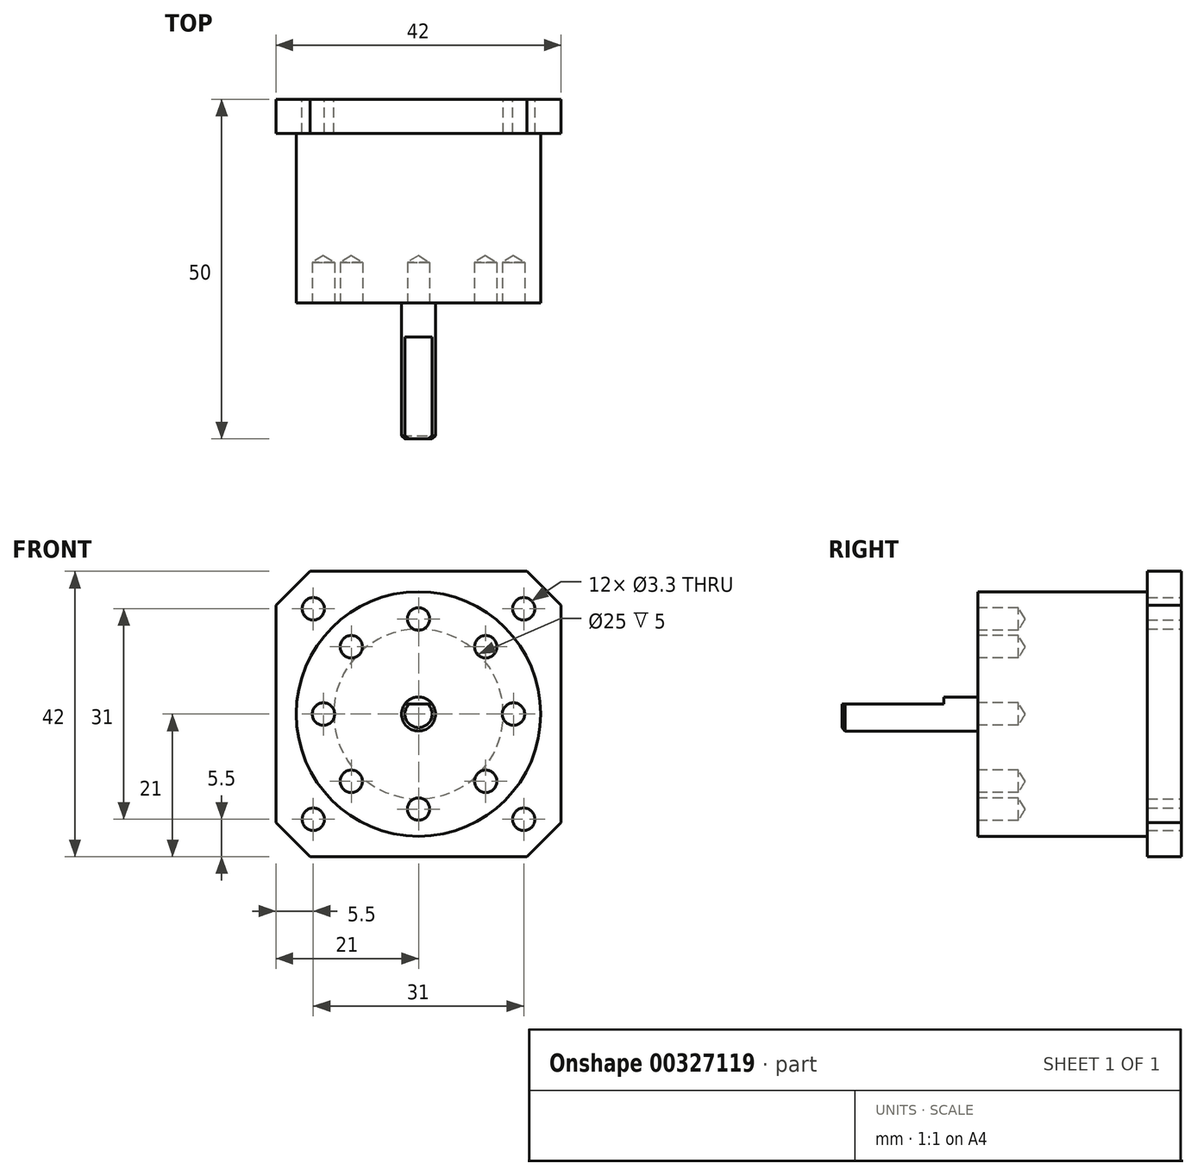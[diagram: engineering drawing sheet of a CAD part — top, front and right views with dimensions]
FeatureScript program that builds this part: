
annotation { "Feature Type Name" : "Feature", "Feature Type Description" : "" }
export const myFeature = defineFeature(function(context is Context, id is Id, definition is map)
    precondition{}
    {
        {
            var Q0;
            Q0=qCreatedBy(makeId("Front.planeOp"),FACE);
            var sketch = newSketch(context, id + "F0", { "sketchPlane" : qUnion([Q0])});
            skLineSegment(sketch, "E0.bottom", {"start": v(21, 21) * mm, "end": v(-21, 21) * mm});
            skLineSegment(sketch, "E0.top", {"start": v(21, -21) * mm, "end": v(-21, -21) * mm});
            skLineSegment(sketch, "E0.left", {"start": v(21, 21) * mm, "end": v(21, -21) * mm});
            skLineSegment(sketch, "E0.right", {"start": v(-21, 21) * mm, "end": v(-21, -21) * mm});
            skPoint(sketch, "E0.middle", {"position": v(0, 0) * mm});
            skLineSegment(sketch, "E1.bottom", {"start": v(-15.5, 15.5) * mm, "end": v(15.5, 15.5) * mm, "construction": true});
            skLineSegment(sketch, "E1.top", {"start": v(-15.5, -15.5) * mm, "end": v(15.5, -15.5) * mm, "construction": true});
            skLineSegment(sketch, "E1.left", {"start": v(-15.5, 15.5) * mm, "end": v(-15.5, -15.5) * mm, "construction": true});
            skLineSegment(sketch, "E1.right", {"start": v(15.5, 15.5) * mm, "end": v(15.5, -15.5) * mm, "construction": true});
            skCircle(sketch, "E2", {"center": v(0, 0) * mm, "radius": 12.5 * mm});
            skSolve(sketch);
        }
        {
            var Q0;
            Q0=makeQuery(id+"F0.imprint","IMPRINT",FACE,{"disambiguationData":[TD([[makeQuery(id+"F0.imprint","IMPRINT",EDGE,{"derivedFrom":sQuery(id+"F0.wireOp",EDGE,"E0.bottom")}),1.0]])]});
            extrude(context, id + "F1", {"entities" : qUnion([Q0]), "depth" : 5 * mm});
        }
        {
            var Q0;
            Q0=makeQuery(id+"F1.opExtrude","CAP_FACE",FACE,{"disambiguationData":[OSD([sQuery(id+"F0.wireOp",EDGE,"E0.bottom"),sQuery(id+"F0.wireOp",EDGE,"E0.top"),sQuery(id+"F0.wireOp",EDGE,"E0.left"),sQuery(id+"F0.wireOp",EDGE,"E0.right"),sQuery(id+"F0.wireOp",EDGE,"E2")])],"isStart":false});
            var sketch = newSketch(context, id + "F2", { "sketchPlane" : qUnion([Q0])});
            skCircle(sketch, "E3", {"center": v(0, 0) * mm, "radius": 18 * mm});
            skSolve(sketch);
        }
        {
            var Q0;
            Q0=makeQuery(id+"F2.imprint","IMPRINT",FACE,{"disambiguationData":[TD([[makeQuery(id+"F2.imprint","IMPRINT",EDGE,{"derivedFrom":sQuery(id+"F2.wireOp",EDGE,"E3")}),1.0]])]});
            var Q1;
            Q1=makeQuery(id+"F2.imprint","IMPRINT",FACE,{"disambiguationData":[TD([[makeQuery(id+"F2.imprint","IMPRINT",EDGE,{"derivedFrom":makeQuery(id+"F1.opExtrude","CAP_EDGE",EDGE,{"disambiguationData":[OSD([sQuery(id+"F0.wireOp",EDGE,"E2")])],"isStart":false})}),1.0]])]});
            extrude(context, id + "F3", {"entities" : qUnion([Q0, Q1]), "operationType" : NewBodyOperationType.ADD, "depth" : 25 * mm});
        }
        {
            var Q0;
            Q0=makeQuery(id+"F3.opExtrude","CAP_FACE",FACE,{"disambiguationData":[OSD([sQuery(id+"F2.wireOp",EDGE,"E3")])],"isStart":false});
            var sketch = newSketch(context, id + "F4", { "sketchPlane" : qUnion([Q0])});
            skCircle(sketch, "E4.cCircle", {"center": v(0, 0) * mm, "radius": 14 * mm, "construction": true});
            skLineSegment(sketch, "E4.0", {"start": v(0, 14) * mm, "end": v(14, 0) * mm, "construction": true});
            skLineSegment(sketch, "E4.1", {"start": v(14, 0) * mm, "end": v(0, -14) * mm, "construction": true});
            skLineSegment(sketch, "E4.2", {"start": v(0, -14) * mm, "end": v(-14, 0) * mm, "construction": true});
            skLineSegment(sketch, "E4.3", {"start": v(-14, 0) * mm, "end": v(0, 14) * mm, "construction": true});
            skCircle(sketch, "E5", {"center": v(0, 0) * mm, "radius": 2.5 * mm});
            skLineSegment(sketch, "E6.bottom", {"start": v(9.9, 9.9) * mm, "end": v(-9.9, 9.9) * mm, "construction": true});
            skLineSegment(sketch, "E6.top", {"start": v(9.9, -9.9) * mm, "end": v(-9.9, -9.9) * mm, "construction": true});
            skLineSegment(sketch, "E6.left", {"start": v(9.9, 9.9) * mm, "end": v(9.9, -9.9) * mm, "construction": true});
            skLineSegment(sketch, "E6.right", {"start": v(-9.9, 9.9) * mm, "end": v(-9.9, -9.9) * mm, "construction": true});
            skSolve(sketch);
        }
        {
            var Q0;
            Q0=makeQuery(id+"F4.imprint","IMPRINT",FACE,{"disambiguationData":[TD([[makeQuery(id+"F4.imprint","IMPRINT",EDGE,{"derivedFrom":sQuery(id+"F4.wireOp",EDGE,"E5")}),1.0]])]});
            extrude(context, id + "F5", {"entities" : qUnion([Q0]), "operationType" : NewBodyOperationType.ADD, "depth" : 20 * mm});
        }
        {
            var Q0;
            Q0=makeQuery(id+"F5.opExtrude","CAP_FACE",FACE,{"disambiguationData":[OSD([sQuery(id+"F4.wireOp",EDGE,"E5")])],"isStart":false});
            var sketch = newSketch(context, id + "F6", { "sketchPlane" : qUnion([Q0])});
            skLineSegment(sketch, "E7", {"start": v(2, 1.5) * mm, "end": v(-2, 1.5) * mm});
            skSolve(sketch);
        }
        {
            var Q0;
            {var subQ0=sQuery(id+"F6.wireOp",EDGE,"E7");Q0=makeQuery(id+"F6.imprint","IMPRINT",FACE,{"disambiguationData":[TD([[makeQuery(id+"F6.imprint","IMPRINT",EDGE,{"derivedFrom":subQ0}),-1.0]])]});}
            extrude(context, id + "F7", {"entities" : qUnion([Q0]), "operationType" : NewBodyOperationType.REMOVE, "oppositeDirection" : true, "depth" : 15 * mm});
        }
        {
            var Q0;
            Q0=sQuery(id+"F0.wireOp",VERTEX,"E1.left.start");
            var Q1;
            Q1=sQuery(id+"F0.wireOp",VERTEX,"E1.right.start");
            var Q2;
            Q2=sQuery(id+"F0.wireOp",VERTEX,"E1.left.end");
            var Q3;
            Q3=sQuery(id+"F0.wireOp",VERTEX,"E1.right.end");
            var Q4;
            Q4=makeQuery(id+"F1.opExtrude","SWEPT_BODY",BODY,{"disambiguationData":[OSD([sQuery(id+"F0.wireOp",EDGE,"E0.bottom"),sQuery(id+"F0.wireOp",EDGE,"E0.top"),sQuery(id+"F0.wireOp",EDGE,"E0.left"),sQuery(id+"F0.wireOp",EDGE,"E0.right"),sQuery(id+"F0.wireOp",EDGE,"E2")])]});
            hole(context, id + "F8", {"style" : HoleStyle.SIMPLE, "endStyle" : HoleEndStyle.THROUGH, "oppositeDirection" : true, "standardTappedOrClearance" : lookupTablePath({ "standard" : "ISO", "fit" : "Normal", "size" : "M3", "type" : "Clearance" }), "standardBlindInLast" : lookupTablePath({ "fit" : "Standard", "standard" : "ISO", "size" : "M3", "type" : "Clearance" }), "holeDiameter" : 3.3 * mm, "tappedDepth" : 12 * mm, "tapClearance" : 3, "locations" : qUnion([Q0, Q1, Q2, Q3]), "scope" : qUnion([Q4])});
        }
        {
            var Q0;
            Q0=sQuery(id+"F4.wireOp",VERTEX,"E4.0.start");
            var Q1;
            Q1=sQuery(id+"F4.wireOp",VERTEX,"E4.3.start");
            var Q2;
            Q2=sQuery(id+"F4.wireOp",VERTEX,"E4.2.start");
            var Q3;
            Q3=sQuery(id+"F4.wireOp",VERTEX,"E4.1.start");
            var Q4;
            Q4=sQuery(id+"F4.wireOp",VERTEX,"E6.right.start");
            var Q5;
            Q5=sQuery(id+"F4.wireOp",VERTEX,"E6.right.end");
            var Q6;
            Q6=sQuery(id+"F4.wireOp",VERTEX,"E6.left.end");
            var Q7;
            Q7=sQuery(id+"F4.wireOp",VERTEX,"E6.left.start");
            var Q8;
            Q8=makeQuery(id+"F1.opExtrude","SWEPT_BODY",BODY,{"disambiguationData":[OSD([sQuery(id+"F0.wireOp",EDGE,"E0.bottom"),sQuery(id+"F0.wireOp",EDGE,"E0.top"),sQuery(id+"F0.wireOp",EDGE,"E0.left"),sQuery(id+"F0.wireOp",EDGE,"E0.right"),sQuery(id+"F0.wireOp",EDGE,"E2")])]});
            hole(context, id + "F9", {"style" : HoleStyle.SIMPLE, "endStyle" : HoleEndStyle.BLIND, "standardTappedOrClearance" : lookupTablePath({ "standard" : "ISO", "fit" : "Normal", "size" : "M3", "type" : "Clearance" }), "standardBlindInLast" : lookupTablePath({ "fit" : "Standard", "standard" : "ISO", "size" : "M3", "type" : "Clearance" }), "holeDiameter" : 3.3 * mm, "holeDepth" : 6 * mm, "tappedDepth" : 12 * mm, "tapClearance" : 3, "locations" : qUnion([Q0, Q1, Q2, Q3, Q4, Q5, Q6, Q7]), "scope" : qUnion([Q8])});
        }
        {
            var Q0;
            Q0=makeQuery(id+"F1.opExtrude","SWEPT_EDGE",EDGE,{"disambiguationData":[OSD([sQuery(id+"F0.wireOp",EDGE,"E0.bottom"),sQuery(id+"F0.wireOp",EDGE,"E0.right")])]});
            var Q1;
            Q1=makeQuery(id+"F1.opExtrude","SWEPT_EDGE",EDGE,{"disambiguationData":[OSD([sQuery(id+"F0.wireOp",EDGE,"E0.bottom"),sQuery(id+"F0.wireOp",EDGE,"E0.left")])]});
            var Q2;
            Q2=makeQuery(id+"F1.opExtrude","SWEPT_EDGE",EDGE,{"disambiguationData":[OSD([sQuery(id+"F0.wireOp",EDGE,"E0.top"),sQuery(id+"F0.wireOp",EDGE,"E0.right")])]});
            var Q3;
            Q3=makeQuery(id+"F1.opExtrude","SWEPT_EDGE",EDGE,{"disambiguationData":[OSD([sQuery(id+"F0.wireOp",EDGE,"E0.top"),sQuery(id+"F0.wireOp",EDGE,"E0.left")])]});
            chamfer(context, id + "F10", {"entities" : qUnion([Q0, Q1, Q2, Q3]), "width" : 5 * mm, "tangentPropagation" : true});
        }
        {
            var Q0;
            Q0=makeQuery(id+"F5.opExtrude","CAP_EDGE",EDGE,{"disambiguationData":[OSD([sQuery(id+"F4.wireOp",EDGE,"E5")])],"isStart":false});
            var Q1;
            Q1=makeQuery(id+"F7.boolean.opBoolean","COPY",EDGE,{"derivedFrom":makeQuery(id+"F7.opExtrude","CAP_EDGE",EDGE,{"disambiguationData":[OSD([sQuery(id+"F4.wireOp",EDGE,"E5")])],"isStart":false})});
            chamfer(context, id + "F11", {"entities" : qUnion([Q0, Q1]), "width" : 0.5 * mm, "tangentPropagation" : true});
        }
    });
